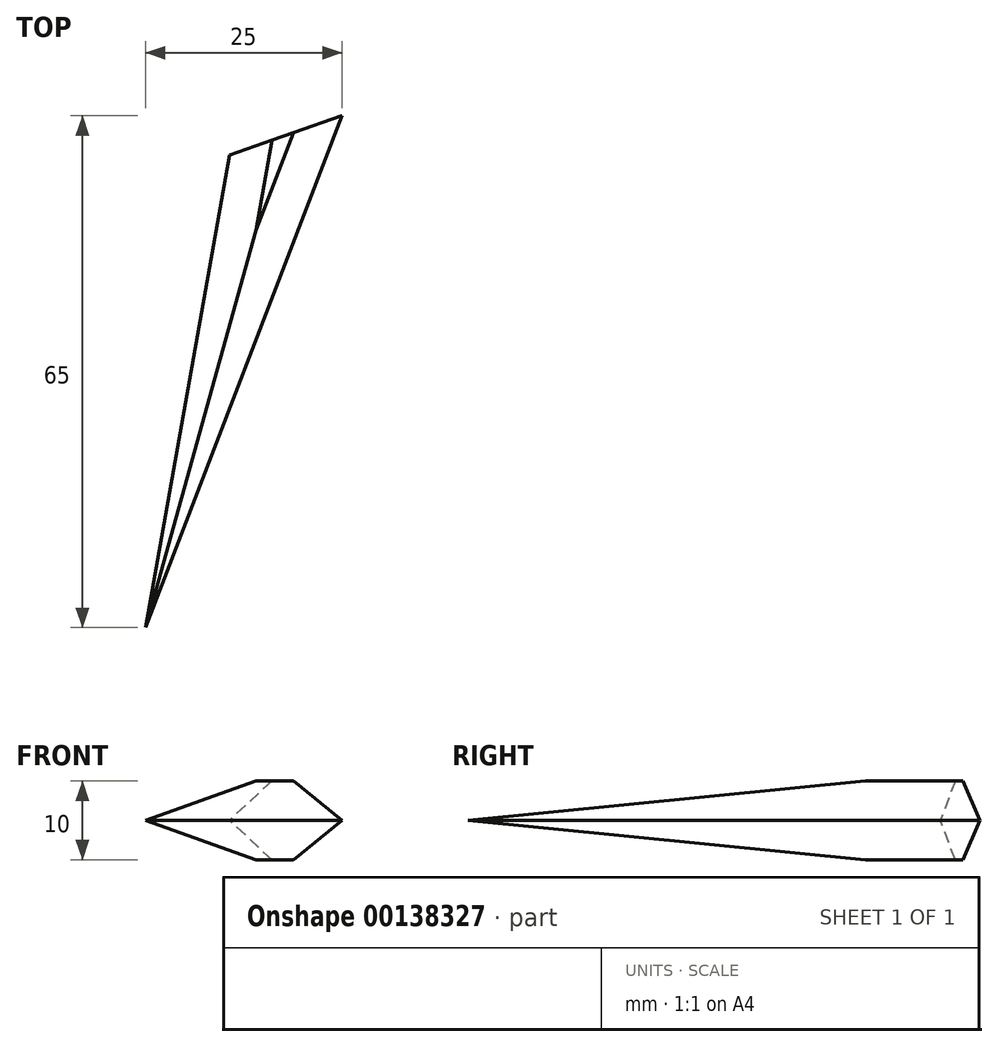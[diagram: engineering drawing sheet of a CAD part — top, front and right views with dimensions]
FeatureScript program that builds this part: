
annotation { "Feature Type Name" : "Feature", "Feature Type Description" : "" }
export const myFeature = defineFeature(function(context is Context, id is Id, definition is map)
    precondition{}
    {
        {
            var Q0;
            Q0=qCreatedBy(makeId("Top.planeOp"),FACE);
            var sketch = newSketch(context, id + "F0", { "sketchPlane" : qUnion([Q0])});
            skLineSegment(sketch, "E0", {"start": v(-40.77, 36.84) * mm, "end": v(-26.44, 41.84) * mm});
            skLineSegment(sketch, "E1", {"start": v(-26.44, 41.84) * mm, "end": v(-51.44, -23.16) * mm});
            skLineSegment(sketch, "E2", {"start": v(-51.44, -23.16) * mm, "end": v(-40.77, 36.84) * mm});
            skSolve(sketch);
        }
        {
            var Q0;
            Q0 = qSketchRegion(id + "F0", true);
            extrude(context, id + "F1", {"entities" : qUnion([Q0]), "depth" : 10 * mm});
        }
        {
            var Q0;
            Q0=makeQuery(id+"F1.opExtrude","CAP_EDGE",EDGE,{"disambiguationData":[OSD([sQuery(id+"F0.wireOp",EDGE,"E2")])],"isStart":false});
            var Q1;
            Q1=makeQuery(id+"F1.opExtrude","CAP_EDGE",EDGE,{"disambiguationData":[OSD([sQuery(id+"F0.wireOp",EDGE,"E1")])],"isStart":false});
            var Q2;
            Q2=makeQuery(id+"F1.opExtrude","CAP_EDGE",EDGE,{"disambiguationData":[OSD([sQuery(id+"F0.wireOp",EDGE,"E2")])],"isStart":true});
            var Q3;
            Q3=makeQuery(id+"F1.opExtrude","CAP_EDGE",EDGE,{"disambiguationData":[OSD([sQuery(id+"F0.wireOp",EDGE,"E1")])],"isStart":true});
            chamfer(context, id + "F2", {"entities" : qUnion([Q0, Q1, Q2, Q3]), "width" : 5 * mm, "tangentPropagation" : true});
        }
    });
